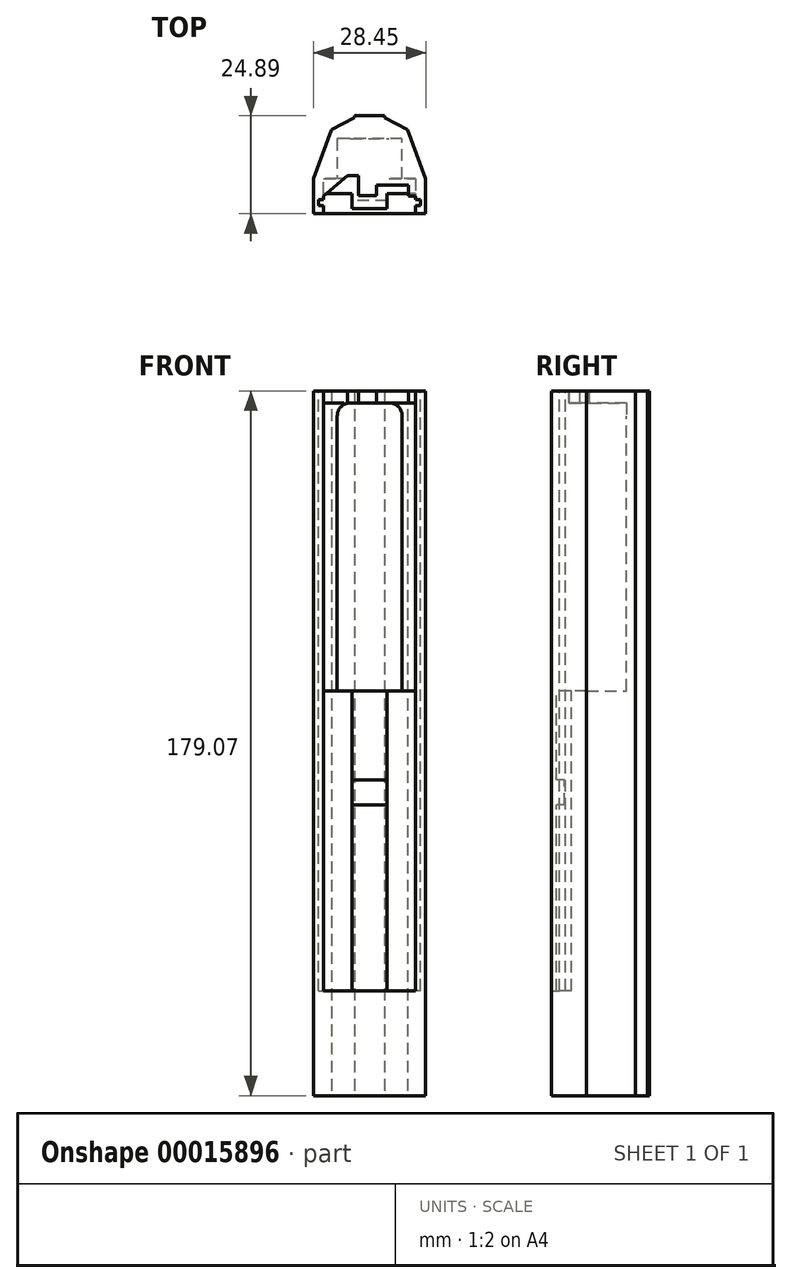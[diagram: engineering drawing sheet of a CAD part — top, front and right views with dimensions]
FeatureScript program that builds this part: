
annotation { "Feature Type Name" : "Feature", "Feature Type Description" : "" }
export const myFeature = defineFeature(function(context is Context, id is Id, definition is map)
    precondition{}
    {
        {
            var Q0;
            Q0=qCreatedBy(makeId("Top.planeOp"),FACE);
            var sketch = newSketch(context, id + "F0", { "sketchPlane" : qUnion([Q0])});
            skLineSegment(sketch, "E0", {"start": v(0, 0) * mm, "end": v(0, 8.9) * mm});
            skLineSegment(sketch, "E1", {"start": v(0, 8.89) * mm, "end": v(4.57, 21.34) * mm});
            skLineSegment(sketch, "E2", {"start": v(4.57, 21.34) * mm, "end": v(10.41, 24.38) * mm});
            skLineSegment(sketch, "E3", {"start": v(10.41, 24.38) * mm, "end": v(10.41, 24.9) * mm});
            skLineSegment(sketch, "E4", {"start": v(10.41, 24.9) * mm, "end": v(18.03, 24.9) * mm});
            skLineSegment(sketch, "E5", {"start": v(18.03, 24.9) * mm, "end": v(18.03, 24.38) * mm});
            skLineSegment(sketch, "E6", {"start": v(18.03, 24.38) * mm, "end": v(23.88, 21.34) * mm});
            skLineSegment(sketch, "E7", {"start": v(23.88, 21.34) * mm, "end": v(28.45, 8.9) * mm});
            skLineSegment(sketch, "E8", {"start": v(28.45, 8.9) * mm, "end": v(28.45, 0) * mm});
            skLineSegment(sketch, "E9", {"start": v(28.45, 0) * mm, "end": v(0, 0) * mm});
            skLineSegment(sketch, "E10", {"start": v(4.57, 21.34) * mm, "end": v(23.88, 21.34) * mm, "construction": true});
            skLineSegment(sketch, "E11", {"start": v(10.41, 24.38) * mm, "end": v(18.03, 24.38) * mm});
            skLineSegment(sketch, "E12", {"start": v(14.22, 0) * mm, "end": v(14.22, 24.38) * mm, "construction": true});
            skSolve(sketch);
        }
        {
            var Q0;
            Q0 = qSketchRegion(id + "F0", true);
            extrude(context, id + "F1", {"entities" : qUnion([Q0]), "depth" : 179.07 * mm});
        }
        {
            var Q0;
            Q0=makeQuery(id+"F1.opExtrude","CAP_FACE",FACE,{"disambiguationData":[OSD([sQuery(id+"F0.wireOp",EDGE,"E0"),sQuery(id+"F0.wireOp",EDGE,"E1"),sQuery(id+"F0.wireOp",EDGE,"E2"),sQuery(id+"F0.wireOp",EDGE,"E3"),sQuery(id+"F0.wireOp",EDGE,"E4"),sQuery(id+"F0.wireOp",EDGE,"E5"),sQuery(id+"F0.wireOp",EDGE,"E6"),sQuery(id+"F0.wireOp",EDGE,"E7"),sQuery(id+"F0.wireOp",EDGE,"E8"),sQuery(id+"F0.wireOp",EDGE,"E9")])],"isStart":false});
            var sketch = newSketch(context, id + "F2", { "sketchPlane" : qUnion([Q0])});
            skLineSegment(sketch, "E13", {"start": v(2.54, 0) * mm, "end": v(2.54, 2.03) * mm});
            skLineSegment(sketch, "E14", {"start": v(2.54, 2.03) * mm, "end": v(1.27, 2.03) * mm});
            skLineSegment(sketch, "E15", {"start": v(1.27, 2.03) * mm, "end": v(1.27, 3.56) * mm});
            skLineSegment(sketch, "E16", {"start": v(1.27, 3.56) * mm, "end": v(2.54, 3.56) * mm});
            skLineSegment(sketch, "E17", {"start": v(2.54, 3.56) * mm, "end": v(2.54, 4.44) * mm});
            skLineSegment(sketch, "E18", {"start": v(2.54, 4.44) * mm, "end": v(8.64, 9.65) * mm});
            skLineSegment(sketch, "E19", {"start": v(8.64, 9.65) * mm, "end": v(11.43, 9.65) * mm});
            skLineSegment(sketch, "E20", {"start": v(11.43, 9.65) * mm, "end": v(11.43, 4.57) * mm});
            skLineSegment(sketch, "E21", {"start": v(11.43, 4.57) * mm, "end": v(16, 4.57) * mm});
            skLineSegment(sketch, "E22", {"start": v(16, 4.57) * mm, "end": v(16, 7.24) * mm});
            skLineSegment(sketch, "E23", {"start": v(16, 7.24) * mm, "end": v(24.13, 7.24) * mm});
            skLineSegment(sketch, "E24", {"start": v(24.13, 7.24) * mm, "end": v(24.13, 4.45) * mm});
            skLineSegment(sketch, "E25", {"start": v(24.13, 4.45) * mm, "end": v(25.9, 4.45) * mm});
            skLineSegment(sketch, "E26", {"start": v(25.9, 4.45) * mm, "end": v(25.9, 3.56) * mm});
            skLineSegment(sketch, "E27", {"start": v(25.9, 3.56) * mm, "end": v(27.18, 3.56) * mm});
            skLineSegment(sketch, "E28", {"start": v(27.18, 3.56) * mm, "end": v(27.18, 2.03) * mm});
            skLineSegment(sketch, "E29", {"start": v(27.18, 2.03) * mm, "end": v(25.9, 2.03) * mm});
            skLineSegment(sketch, "E30", {"start": v(25.9, 2.03) * mm, "end": v(25.9, 0) * mm});
            skLineSegment(sketch, "E31", {"start": v(25.9, 0) * mm, "end": v(2.54, 0) * mm});
            skSolve(sketch);
        }
        {
            var Q0;
            Q0=makeQuery(id+"F2.imprint","IMPRINT",FACE,{"disambiguationData":[TD([[makeQuery(id+"F2.imprint","IMPRINT",EDGE,{"derivedFrom":sQuery(id+"F2.wireOp",EDGE,"E13")}),-1.0]])]});
            extrude(context, id + "F3", {"entities" : qUnion([Q0]), "operationType" : NewBodyOperationType.REMOVE, "oppositeDirection" : true, "depth" : 76.2 * mm});
        }
        {
            var Q0;
            Q0=makeQuery(id+"F1.opExtrude","CAP_FACE",FACE,{"disambiguationData":[OSD([sQuery(id+"F0.wireOp",EDGE,"E0"),sQuery(id+"F0.wireOp",EDGE,"E1"),sQuery(id+"F0.wireOp",EDGE,"E2"),sQuery(id+"F0.wireOp",EDGE,"E3"),sQuery(id+"F0.wireOp",EDGE,"E4"),sQuery(id+"F0.wireOp",EDGE,"E5"),sQuery(id+"F0.wireOp",EDGE,"E6"),sQuery(id+"F0.wireOp",EDGE,"E7"),sQuery(id+"F0.wireOp",EDGE,"E8"),sQuery(id+"F0.wireOp",EDGE,"E9")])],"isStart":false});
            cPlane(context, id + "F4", {"entities" : qUnion([Q0]), "cplaneType" : CPlaneType.OFFSET, "offset" : 3.05 * mm, "oppositeDirection" : true, "width" : 152.4 * mm, "height" : 152.4 * mm});
        }
        {
            var Q0;
            Q0=qCreatedBy(id+"F4.planeOp",FACE);
            var sketch = newSketch(context, id + "F5", { "sketchPlane" : qUnion([Q0])});
            skLineSegment(sketch, "E32", {"start": v(2.54, 0) * mm, "end": v(2.54, 8.9) * mm});
            skLineSegment(sketch, "E33", {"start": v(2.54, 8.9) * mm, "end": v(5.97, 8.9) * mm});
            skLineSegment(sketch, "E34", {"start": v(5.97, 8.9) * mm, "end": v(5.97, 19.05) * mm});
            skLineSegment(sketch, "E35", {"start": v(5.97, 19.05) * mm, "end": v(22.48, 19.05) * mm});
            skLineSegment(sketch, "E36", {"start": v(22.48, 19.05) * mm, "end": v(22.48, 8.9) * mm});
            skLineSegment(sketch, "E37", {"start": v(22.48, 8.9) * mm, "end": v(25.9, 8.9) * mm});
            skLineSegment(sketch, "E38", {"start": v(25.9, 8.9) * mm, "end": v(25.9, 0) * mm});
            skLineSegment(sketch, "E39", {"start": v(25.9, 0) * mm, "end": v(2.54, 0) * mm});
            skSolve(sketch);
        }
        {
            var Q0;
            Q0 = qSketchRegion(id + "F5", true);
            var Q1;
            Q1=makeQuery(id+"F3.boolean.opBoolean","COPY",FACE,{"derivedFrom":makeQuery(id+"F3.opExtrude","CAP_FACE",FACE,{"disambiguationData":[OSD([sQuery(id+"F2.wireOp",EDGE,"E13"),sQuery(id+"F2.wireOp",EDGE,"E14"),sQuery(id+"F2.wireOp",EDGE,"E15"),sQuery(id+"F2.wireOp",EDGE,"E16"),sQuery(id+"F2.wireOp",EDGE,"E17"),sQuery(id+"F2.wireOp",EDGE,"E18"),sQuery(id+"F2.wireOp",EDGE,"E19"),sQuery(id+"F2.wireOp",EDGE,"E20"),sQuery(id+"F2.wireOp",EDGE,"E21"),sQuery(id+"F2.wireOp",EDGE,"E22"),sQuery(id+"F2.wireOp",EDGE,"E23"),sQuery(id+"F2.wireOp",EDGE,"E24"),sQuery(id+"F2.wireOp",EDGE,"E25"),sQuery(id+"F2.wireOp",EDGE,"E26"),sQuery(id+"F2.wireOp",EDGE,"E27"),sQuery(id+"F2.wireOp",EDGE,"E28"),sQuery(id+"F2.wireOp",EDGE,"E29"),sQuery(id+"F2.wireOp",EDGE,"E30"),sQuery(id+"F2.wireOp",EDGE,"E31")])],"isStart":false})});
            extrude(context, id + "F6", {"entities" : qUnion([Q0]), "operationType" : NewBodyOperationType.REMOVE, "endBound" : BoundingType.UP_TO_SURFACE, "oppositeDirection" : true, "endBoundEntityFace" : qUnion([Q1]), "depth" : 25.4 * mm});
        }
        {
            var Q0;
            Q0=makeQuery(id+"F6.boolean.opBoolean","COPY",EDGE,{"derivedFrom":makeQuery(id+"F6.opExtrude","CAP_EDGE",EDGE,{"disambiguationData":[OSD([sQuery(id+"F5.wireOp",EDGE,"E36")])],"isStart":true})});
            var Q1;
            Q1=makeQuery(id+"F6.boolean.opBoolean","COPY",EDGE,{"derivedFrom":makeQuery(id+"F6.opExtrude","CAP_EDGE",EDGE,{"disambiguationData":[OSD([sQuery(id+"F5.wireOp",EDGE,"E34")])],"isStart":true})});
            fillet(context, id + "F7", {"entities" : qUnion([Q0, Q1]), "radius" : 3.3 * mm, "tangentPropagation" : true, "allowEdgeOverflow" : false});
        }
        {
            var Q0;
            {var subQ0=sQuery(id+"F2.wireOp",EDGE,"E31");var subQ1=sQuery(id+"F2.wireOp",EDGE,"E30");var subQ2=sQuery(id+"F2.wireOp",EDGE,"E29");var subQ3=sQuery(id+"F2.wireOp",EDGE,"E28");var subQ4=sQuery(id+"F2.wireOp",EDGE,"E27");var subQ5=sQuery(id+"F2.wireOp",EDGE,"E26");var subQ6=sQuery(id+"F2.wireOp",EDGE,"E25");var subQ7=sQuery(id+"F2.wireOp",EDGE,"E24");var subQ8=sQuery(id+"F2.wireOp",EDGE,"E23");var subQ9=sQuery(id+"F2.wireOp",EDGE,"E22");var subQ10=sQuery(id+"F2.wireOp",EDGE,"E21");var subQ11=sQuery(id+"F2.wireOp",EDGE,"E20");var subQ12=sQuery(id+"F2.wireOp",EDGE,"E19");var subQ13=sQuery(id+"F2.wireOp",EDGE,"E18");var subQ14=sQuery(id+"F2.wireOp",EDGE,"E17");var subQ15=sQuery(id+"F2.wireOp",EDGE,"E16");var subQ16=sQuery(id+"F2.wireOp",EDGE,"E15");var subQ17=sQuery(id+"F2.wireOp",EDGE,"E14");var subQ18=sQuery(id+"F2.wireOp",EDGE,"E13");Q0=makeQuery(id+"F6.boolean.opBoolean","MERGE",FACE,{"derivedFrom":[makeQuery(id+"F3.boolean.opBoolean","COPY",FACE,{"derivedFrom":makeQuery(id+"F3.opExtrude","CAP_FACE",FACE,{"disambiguationData":[OSD([subQ18,subQ17,subQ16,subQ15,subQ14,subQ13,subQ12,subQ11,subQ10,subQ9,subQ8,subQ7,subQ6,subQ5,subQ4,subQ3,subQ2,subQ1,subQ0])],"isStart":false})}),makeQuery(id+"F6.opExtrude","CAP_FACE",FACE,{"disambiguationData":[OSD([subQ18,subQ17,subQ16,subQ15,subQ14,subQ13,subQ12,subQ11,subQ10,subQ9,subQ8,subQ7,subQ6,subQ5,subQ4,subQ3,subQ2,subQ1,subQ0])],"isStart":false})]});}
            var sketch = newSketch(context, id + "F8", { "sketchPlane" : qUnion([Q0])});
            skLineSegment(sketch, "E40.0.0", {"start": v(2.54, 2.03) * mm, "end": v(2.54, 0) * mm});
            skLineSegment(sketch, "E40.0.2", {"start": v(2.54, 0) * mm, "end": v(2.54, 2.03) * mm});
            skLineSegment(sketch, "E41.1.0", {"start": v(25.9, 0) * mm, "end": v(25.9, 2.03) * mm});
            skLineSegment(sketch, "E41.1.2", {"start": v(25.9, 2.03) * mm, "end": v(25.9, 0) * mm});
            skLineSegment(sketch, "E42.2.0", {"start": v(27.18, 3.56) * mm, "end": v(25.9, 3.56) * mm});
            skLineSegment(sketch, "E42.2.2", {"start": v(25.9, 3.56) * mm, "end": v(27.18, 3.56) * mm});
            skLineSegment(sketch, "E42.3.0", {"start": v(27.18, 2.03) * mm, "end": v(27.18, 3.56) * mm});
            skLineSegment(sketch, "E42.3.2", {"start": v(27.18, 3.56) * mm, "end": v(27.18, 2.03) * mm});
            skLineSegment(sketch, "E42.4.0", {"start": v(25.9, 2.03) * mm, "end": v(27.18, 2.03) * mm});
            skLineSegment(sketch, "E42.4.2", {"start": v(27.18, 2.03) * mm, "end": v(25.9, 2.03) * mm});
            skLineSegment(sketch, "E42.5.0", {"start": v(1.27, 3.56) * mm, "end": v(1.27, 2.03) * mm});
            skLineSegment(sketch, "E42.5.2", {"start": v(1.27, 2.03) * mm, "end": v(1.27, 3.56) * mm});
            skLineSegment(sketch, "E42.6.0", {"start": v(2.54, 3.56) * mm, "end": v(1.27, 3.56) * mm});
            skLineSegment(sketch, "E42.6.2", {"start": v(1.27, 3.56) * mm, "end": v(2.54, 3.56) * mm});
            skLineSegment(sketch, "E42.7.0", {"start": v(1.27, 2.03) * mm, "end": v(2.54, 2.03) * mm});
            skLineSegment(sketch, "E42.7.2", {"start": v(2.54, 2.03) * mm, "end": v(1.27, 2.03) * mm});
            skLineSegment(sketch, "E43", {"start": v(25.9, 3.56) * mm, "end": v(25.9, 5.08) * mm});
            skLineSegment(sketch, "E44", {"start": v(25.9, 5.08) * mm, "end": v(18.67, 5.08) * mm});
            skLineSegment(sketch, "E45", {"start": v(2.54, 5.08) * mm, "end": v(2.54, 3.56) * mm});
            skLineSegment(sketch, "E46.top", {"start": v(18.67, 1.27) * mm, "end": v(9.78, 1.27) * mm});
            skLineSegment(sketch, "E46.left", {"start": v(18.67, 5.08) * mm, "end": v(18.67, 1.27) * mm});
            skLineSegment(sketch, "E46.right", {"start": v(9.78, 5.08) * mm, "end": v(9.78, 1.27) * mm});
            skLineSegment(sketch, "E47", {"start": v(25.9, 0) * mm, "end": v(2.54, 0) * mm});
            skLineSegment(sketch, "E48.trimOffspring", {"start": v(9.78, 5.08) * mm, "end": v(2.54, 5.08) * mm});
            skSolve(sketch);
        }
        {
            var Q0;
            Q0 = qSketchRegion(id + "F8", true);
            extrude(context, id + "F9", {"entities" : qUnion([Q0]), "operationType" : NewBodyOperationType.REMOVE, "oppositeDirection" : true, "depth" : 76.2 * mm});
        }
        {
            var Q0;
            Q0=makeQuery(id+"F9.boolean.opBoolean","COPY",FACE,{"derivedFrom":makeQuery(id+"F9.opExtrude","SWEPT_FACE",FACE,{"disambiguationData":[OSD([sQuery(id+"F8.wireOp",EDGE,"E46.top")])]})});
            var sketch = newSketch(context, id + "F10", { "sketchPlane" : qUnion([Q0])});
            skLineSegment(sketch, "E49.bottom", {"start": v(18.67, 80.26) * mm, "end": v(9.78, 80.26) * mm});
            skLineSegment(sketch, "E49.top", {"start": v(18.67, 73.91) * mm, "end": v(9.78, 73.91) * mm});
            skLineSegment(sketch, "E49.left", {"start": v(18.67, 80.26) * mm, "end": v(18.67, 73.91) * mm});
            skLineSegment(sketch, "E49.right", {"start": v(9.78, 80.26) * mm, "end": v(9.78, 73.91) * mm});
            skLineSegment(sketch, "E50.0", {"start": v(11.43, 179.07) * mm, "end": v(16, 179.07) * mm, "construction": true});
            skSolve(sketch);
        }
        {
            var Q0;
            Q0 = qSketchRegion(id + "F10", true);
            extrude(context, id + "F11", {"entities" : qUnion([Q0]), "operationType" : NewBodyOperationType.REMOVE, "oppositeDirection" : true, "depth" : 2.03 * mm});
        }
    });
